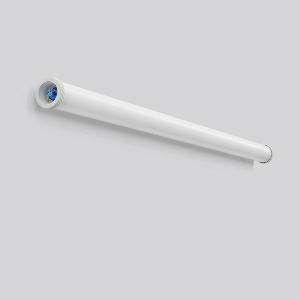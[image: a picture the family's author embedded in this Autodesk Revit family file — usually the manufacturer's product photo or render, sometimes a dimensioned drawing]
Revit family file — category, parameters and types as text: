
# Revit family: planox_tube_farm_601072_002_5_84f7
name_source: partatom
category: Lighting Fixtures
units: mm (PartAtom-declared; Revit-internal decimal feet)

## family parameters
Cut with Voids When Loaded = No
Host = Face
Light Source = No
Part Type = Normal
Room Calculation Point = No
Round Connector Dimension = Use Diameter
Shared = No

## types (1)
- PLANOX TUBE FARM (1 x LED Modul 840, 10000 lm, 4000)
    Apparent Load = 62 VA
    CIE Flux Codes = 44 74 91 92 100
    Color Rendering = 80
    Color Temperature = 4000
    Default Elevation = 1800 mm
    Description = Series: PLANOX TUBE FARM
Ammonia-resistant protective tube luminaire for tough requirements. Rack made of sheet steel, white powder coated. End caps made of plastic (polyamide) grey. Diffuser made of UV-resistant plastic (PMMA), opal. Symmetrical light distribution. Homogeneous light distribution. With accessories for wall, ceiling or pendant mounting. Driver integrated. Easy installation with the Plug+Play Wieland RST CLASSIC plug-in system. Mounting set must be ordered separately. Luminaire with limited surface temperature in accordance with EN 60598-2-24 for use in environments in which a deposit of conductive dust on the luminaire can be expected. Ammonia resistant : Suitable for the use in stables with livestock and agricultural side areas. Environmentally friendly and resource-saving due to replaceable components. 
Colour: white
Diameter: 78 mm
Length: 1564 mm
Lamp: LED
Socket: without socket
Colour temperature: 4000K
Colour rendering index (CRI): 83
System power: 62 W
Rated luminous flux: 10000 lm
Luminous efficiency: 161 lm/W
Control gear: Regulated power supply
Protection class: I
Type of protection: IP 67
    Height = 0 mm  [stored 0 ft]
    Lamp = 1 x LED Modul 840
    Lamp Light Flux = 10000 lm
    Lamp count = 1
    Length = 1564 mm
    Lifetime = 50000 h
    Luminous efficacy = 161 lm/W
    Manufacturer = RZB
    ModVariant = No
    Model = 601072.002.5
    Mounting Place = Ceiling
    Mounting Type = Surface mounted
    Number of Poles = 1
    OnlyDefault = Yes
    Power Factor = 1
    Product Name = PLANOX TUBE FARM
    Product group = Surface mounted luminaires for moist/humid enviroments
    ProductGroupID = 308
    Protection Class = Protection class I
    Protection Degree = Degree of protection
    RLX_Detail_Level = 1
    RLX_Emergency_Light_Flux = 0 lm
    RLX_Emergency_Type = 0
    RLX_Emergency_Type_DB = No
    RlxData = <blob elided: 34437 chars, md5=e56e75b9>
    Socket = socket
    Standby Power = 0 W
    System Light Flux = 10000 lm
    System Power = 62 W
    Type Comments = Product without accessories
    Type Image = 601072.002.5.jpg
    URL = http://relux.com
    VarID = ---
    Voltage = 0 V
    Weight = 0.00 kg
    Width = 0 mm  [stored 0 ft]

note: [stored X ft] marks values corroborated as IEEE doubles in the binary element streams (Revit-internal decimal feet)

## geometry (parser evidence)
native form markers: Blend x4, Sweep x12
no freeform markers — native parametric forms only
